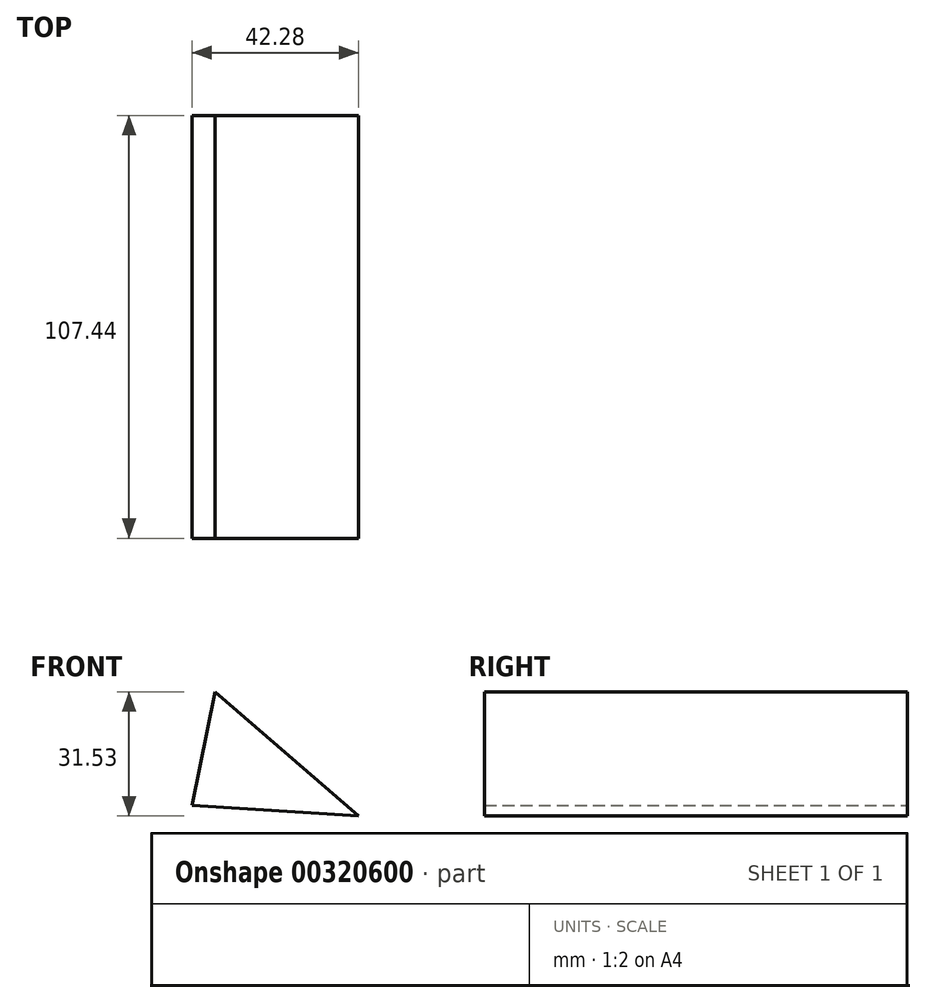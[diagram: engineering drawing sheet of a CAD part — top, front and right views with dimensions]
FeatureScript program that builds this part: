
annotation { "Feature Type Name" : "Feature", "Feature Type Description" : "" }
export const myFeature = defineFeature(function(context is Context, id is Id, definition is map)
    precondition{}
    {
        {
            var Q0;
            Q0=qCreatedBy(makeId("Front.planeOp"),FACE);
            var sketch = newSketch(context, id + "F0", { "sketchPlane" : qUnion([Q0])});
            skLineSegment(sketch, "E0", {"start": v(-20.96, 26.75) * mm, "end": v(-26.75, -2.1) * mm});
            skLineSegment(sketch, "E1", {"start": v(-20.96, 26.75) * mm, "end": v(15.53, -4.78) * mm});
            skLineSegment(sketch, "E2", {"start": v(15.53, -4.78) * mm, "end": v(-26.75, -2.1) * mm});
            skSolve(sketch);
        }
        {
            var Q0;
            Q0 = qSketchRegion(id + "F0", true);
            extrude(context, id + "F1", {"entities" : qUnion([Q0]), "depth" : 107.44 * mm});
        }
    });
